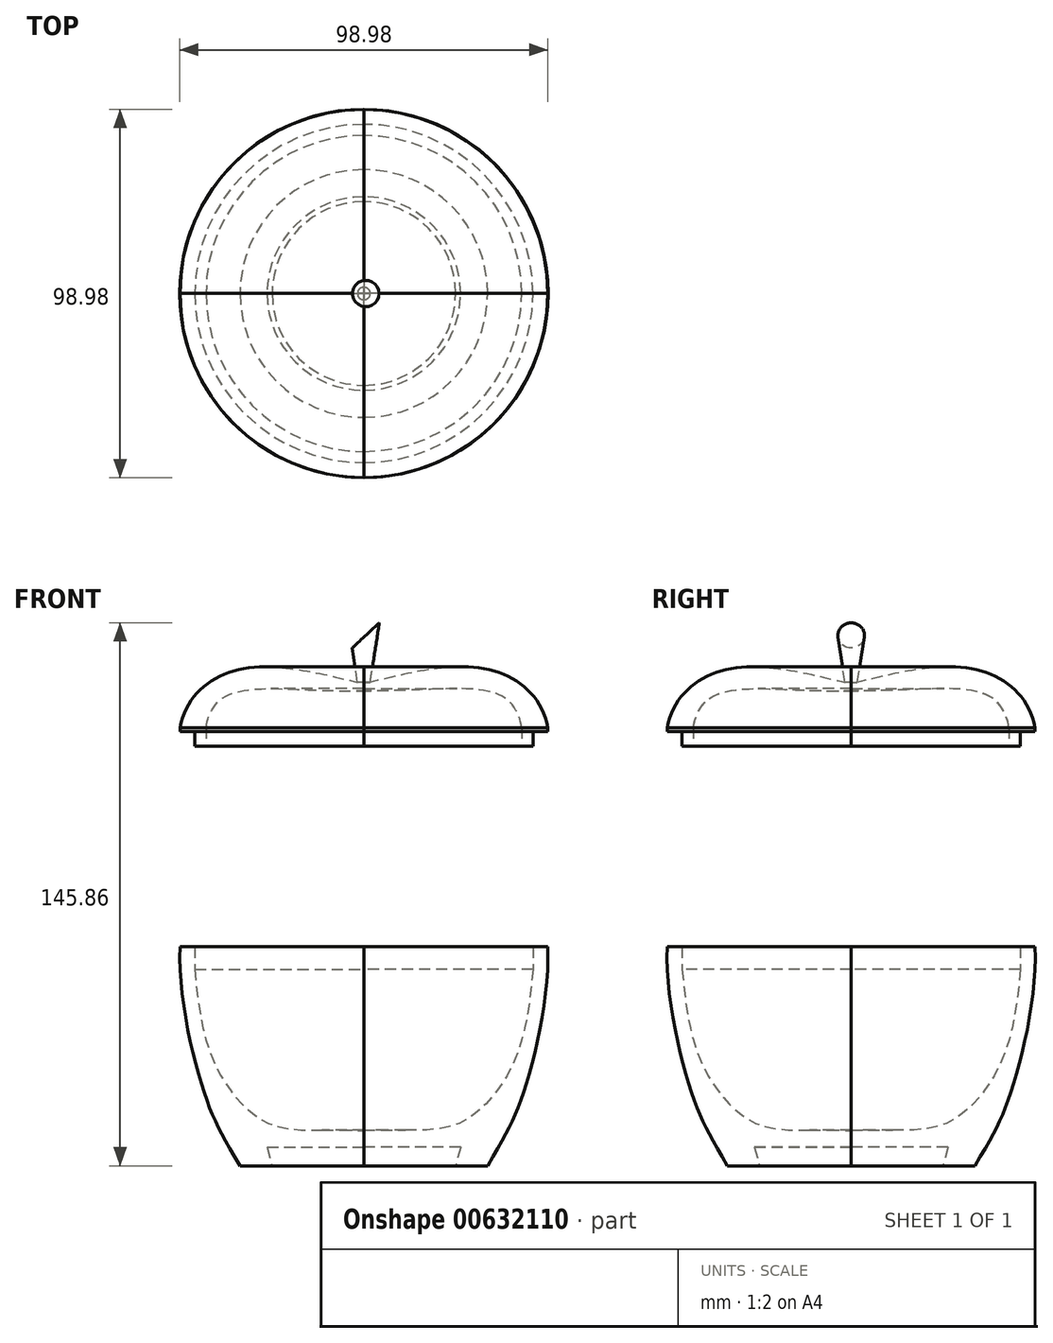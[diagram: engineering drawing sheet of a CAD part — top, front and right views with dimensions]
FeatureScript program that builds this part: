
annotation { "Feature Type Name" : "Feature", "Feature Type Description" : "" }
export const myFeature = defineFeature(function(context is Context, id is Id, definition is map)
    precondition{}
    {
        {
            var Q0;
            Q0=qCreatedBy(makeId("Front.planeOp"),FACE);
            var sketch = newSketch(context, id + "F0", { "sketchPlane" : qUnion([Q0])});
            skLineSegment(sketch, "E0.top", {"start": v(50, 30) * mm, "end": v(-50, 30) * mm, "construction": true});
            skLineSegment(sketch, "E0.left", {"start": v(50, -30) * mm, "end": v(50, 30) * mm, "construction": true});
            skLineSegment(sketch, "E0.right", {"start": v(-50, -30) * mm, "end": v(-50, 30) * mm, "construction": true});
            skPoint(sketch, "E0.middle", {"position": v(0, 0) * mm});
            skLineSegment(sketch, "E1.bottom", {"start": v(50, 82.63) * mm, "end": v(-50, 82.63) * mm, "construction": true});
            skLineSegment(sketch, "E1.left", {"start": v(50, 82.63) * mm, "end": v(50, 112.63) * mm, "construction": true});
            skLineSegment(sketch, "E1.right", {"start": v(-50, 82.63) * mm, "end": v(-50, 112.63) * mm, "construction": true});
            skPoint(sketch, "E1.middle", {"position": v(0, 97.63) * mm});
            skLineSegment(sketch, "E2", {"start": v(0, -24.93) * mm, "end": v(26, -24.93) * mm});
            skLineSegment(sketch, "E3", {"start": v(26, -24.93) * mm, "end": v(24.66, -29.93) * mm});
            skLineSegment(sketch, "E4", {"start": v(24.66, -29.93) * mm, "end": v(33.27, -29.93) * mm});
            skFitSpline(sketch, "E5", {"points": [v(33.27, -29.93) * mm, v(42.67, -10.91) * mm, v(49.44, 28.9) * mm], "startDerivative": vector(35.31, 60.18) * mm, "endDerivative": vector(-2.9, 68.51) * mm});
            skLineSegment(sketch, "E6", {"start": v(49.44, 28.9) * mm, "end": v(45.44, 28.9) * mm});
            skLineSegment(sketch, "E7", {"start": v(45.44, 28.9) * mm, "end": v(45.44, 22.9) * mm});
            skFitSpline(sketch, "E8", {"points": [v(45.44, 22.9) * mm, v(37.2, -7.7) * mm, v(25.51, -18.55) * mm, v(0, -20.43) * mm], "startDerivative": vector(-10.15, -125.13) * mm, "endDerivative": vector(-112.63, -2.37) * mm});
            skLineSegment(sketch, "E9", {"start": v(0, -20.43) * mm, "end": v(0, -24.93) * mm});
            skFitSpline(sketch, "E10", {"points": [v(49.44, 87.78) * mm, v(33.04, 103.51) * mm, v(1.7, 100) * mm], "startDerivative": vector(-10.7, 55.03) * mm, "endDerivative": vector(-47.99, -11.1) * mm});
            skLineSegment(sketch, "E11", {"start": v(45.44, 86.78) * mm, "end": v(45.44, 82.78) * mm});
            skLineSegment(sketch, "E12", {"start": v(45.44, 82.78) * mm, "end": v(42.44, 82.78) * mm});
            skLineSegment(sketch, "E13", {"start": v(42.44, 82.78) * mm, "end": v(42.44, 87.78) * mm});
            skFitSpline(sketch, "E14", {"points": [v(42.44, 87.78) * mm, v(37.77, 95.85) * mm, v(20.77, 98.18) * mm, v(0, 97.63) * mm], "startDerivative": vector(-5.04, 33.52) * mm, "endDerivative": vector(-56.64, 0.65) * mm});
            skLineSegment(sketch, "E15", {"start": v(49.44, 87.78) * mm, "end": v(49.44, 86.78) * mm});
            skLineSegment(sketch, "E16", {"start": v(49.44, 86.78) * mm, "end": v(45.44, 86.78) * mm});
            skLineSegment(sketch, "E17", {"start": v(0, 64.7) * mm, "end": v(0, 93.23) * mm, "construction": true});
            skLineSegment(sketch, "E18", {"start": v(0, 97.63) * mm, "end": v(0, 115.93) * mm});
            skLineSegment(sketch, "E19", {"start": v(1.7, 100) * mm, "end": v(4.16, 115.93) * mm});
            skLineSegment(sketch, "E20", {"start": v(4.16, 115.93) * mm, "end": v(0, 115.93) * mm});
            skLineSegment(sketch, "E21", {"start": v(-7.28, 105.36) * mm, "end": v(-7.28, 115.93) * mm});
            skLineSegment(sketch, "E22", {"start": v(-7.28, 115.93) * mm, "end": v(0, 115.93) * mm});
            skLineSegment(sketch, "E23", {"start": v(4.16, 115.93) * mm, "end": v(-7.28, 105.36) * mm});
            skLineSegment(sketch, "E24", {"start": v(1.7, 100) * mm, "end": v(0, 100) * mm});
            skSolve(sketch);
        }
        {
            var Q0;
            Q0=qCreatedBy(makeId("Top.planeOp"),FACE);
            var sketch = newSketch(context, id + "F1", { "sketchPlane" : qUnion([Q0])});
            skLineSegment(sketch, "E25.bottom", {"start": v(0, 0) * mm, "end": v(50, 0) * mm});
            skLineSegment(sketch, "E25.top", {"start": v(0, 50) * mm, "end": v(50, 50) * mm});
            skLineSegment(sketch, "E25.left", {"start": v(0, 0) * mm, "end": v(0, 50) * mm});
            skLineSegment(sketch, "E25.right", {"start": v(50, 0) * mm, "end": v(50, 50) * mm});
            skLineSegment(sketch, "E26.bottom", {"start": v(0, 50) * mm, "end": v(-50, 50) * mm});
            skLineSegment(sketch, "E26.top", {"start": v(0, 0) * mm, "end": v(-50, 0) * mm});
            skLineSegment(sketch, "E26.left", {"start": v(0, 50) * mm, "end": v(0, 0) * mm});
            skLineSegment(sketch, "E26.right", {"start": v(-50, 50) * mm, "end": v(-50, 0) * mm});
            skLineSegment(sketch, "E27.top", {"start": v(0, -50) * mm, "end": v(-50, -50) * mm});
            skLineSegment(sketch, "E27.left", {"start": v(0, 0) * mm, "end": v(0, -50) * mm});
            skLineSegment(sketch, "E27.right", {"start": v(-50, 0) * mm, "end": v(-50, -50) * mm});
            skLineSegment(sketch, "E28.top", {"start": v(0, -50) * mm, "end": v(50, -50) * mm});
            skLineSegment(sketch, "E28.right", {"start": v(50, 0) * mm, "end": v(50, -50) * mm});
            skSolve(sketch);
        }
        {
            var Q0;
            Q0=makeQuery(id+"F1.imprint","IMPRINT",FACE,{"disambiguationData":[TD([[makeQuery(id+"F1.imprint","IMPRINT",EDGE,{"derivedFrom":sQuery(id+"F1.wireOp",EDGE,"E26.bottom")}),1.0]])]});
            var Q1;
            Q1=makeQuery(id+"F1.imprint","IMPRINT",FACE,{"disambiguationData":[TD([[makeQuery(id+"F1.imprint","IMPRINT",EDGE,{"derivedFrom":sQuery(id+"F1.wireOp",EDGE,"E25.bottom")}),-1.0]])]});
            extrude(context, id + "F2", {"entities" : qUnion([Q0, Q1]), "endBound" : BoundingType.SYMMETRIC, "depth" : 250 * mm, "offsetDistance" : 25 * mm});
        }
        {
            var Q0;
            Q0=makeQuery(id+"F1.imprint","IMPRINT",FACE,{"disambiguationData":[TD([[makeQuery(id+"F1.imprint","IMPRINT",EDGE,{"derivedFrom":sQuery(id+"F1.wireOp",EDGE,"E25.top")}),-1.0]])]});
            var Q1;
            Q1=makeQuery(id+"F1.imprint","IMPRINT",FACE,{"disambiguationData":[TD([[makeQuery(id+"F1.imprint","IMPRINT",EDGE,{"derivedFrom":sQuery(id+"F1.wireOp",EDGE,"E26.top")}),1.0]])]});
            extrude(context, id + "F3", {"entities" : qUnion([Q0, Q1]), "endBound" : BoundingType.SYMMETRIC, "depth" : 250 * mm, "offsetDistance" : 25 * mm});
        }
        {
            var Q0;
            Q0=makeQuery(id+"F0.imprint","IMPRINT",FACE,{"disambiguationData":[TD([[makeQuery(id+"F0.imprint","IMPRINT",EDGE,{"derivedFrom":sQuery(id+"F0.wireOp",EDGE,"E10")}),1.0]])]});
            var Q1;
            Q1=makeQuery(id+"F0.imprint","IMPRINT",FACE,{"disambiguationData":[TD([[makeQuery(id+"F0.imprint","IMPRINT",EDGE,{"derivedFrom":sQuery(id+"F0.wireOp",EDGE,"E2")}),1.0]])]});
            var Q2;
            Q2=sQuery(id+"F0.wireOp",EDGE,"E17");
            revolve(context, id + "F4", {"operationType" : NewBodyOperationType.INTERSECT, "entities" : qUnion([Q0, Q1]), "axis" : qUnion([Q2]), "revolveType" : RevolveType.FULL});
        }
        {
            var Q0;
            {var subQ4=sQuery(id+"F0.wireOp",EDGE,"E19");Q0=makeQuery(id+"F0.imprint","IMPRINT",FACE,{"disambiguationData":[TD([[makeQuery(id+"F0.imprint","IMPRINT",EDGE,{"derivedFrom":subQ4}),1.0]])]});}
            var Q1;
            {var subQ0=sQuery(id+"F0.wireOp",EDGE,"E20");Q1=makeQuery(id+"F0.imprint","IMPRINT",FACE,{"disambiguationData":[TD([[makeQuery(id+"F0.imprint","IMPRINT",EDGE,{"derivedFrom":subQ0}),1.0]])]});}
            var Q2;
            Q2=sQuery(id+"F0.wireOp",EDGE,"E17");
            revolve(context, id + "F5", {"entities" : qUnion([Q0, Q1]), "axis" : qUnion([Q2]), "revolveType" : RevolveType.FULL});
        }
        {
            var Q0;
            {var subQ2=sQuery(id+"F0.wireOp",EDGE,"sQN5e2aa-ydus-LUhY-fWXo-VwIeRdBZaAUn");Q0=makeQuery(id+"F0.imprint","IMPRINT",FACE,{"disambiguationData":[TD([[makeQuery(id+"F0.imprint","IMPRINT",EDGE,{"derivedFrom":subQ2}),-1.0]])]});}
            var Q1;
            {var subQ0=sQuery(id+"F0.wireOp",EDGE,"E20");Q1=makeQuery(id+"F0.imprint","IMPRINT",FACE,{"disambiguationData":[TD([[makeQuery(id+"F0.imprint","IMPRINT",EDGE,{"derivedFrom":subQ0}),1.0]])]});}
            var Q2;
            {var subQ4=sQuery(id+"F0.wireOp",EDGE,"E21");Q2=makeQuery(id+"F0.imprint","IMPRINT",FACE,{"disambiguationData":[TD([[makeQuery(id+"F0.imprint","IMPRINT",EDGE,{"derivedFrom":subQ4}),-1.0]])]});}
            extrude(context, id + "F6", {"entities" : qUnion([Q0, Q1, Q2]), "operationType" : NewBodyOperationType.REMOVE, "endBound" : BoundingType.SYMMETRIC, "oppositeDirection" : true, "depth" : 25 * mm, "offsetDistance" : 25 * mm});
        }
    });
